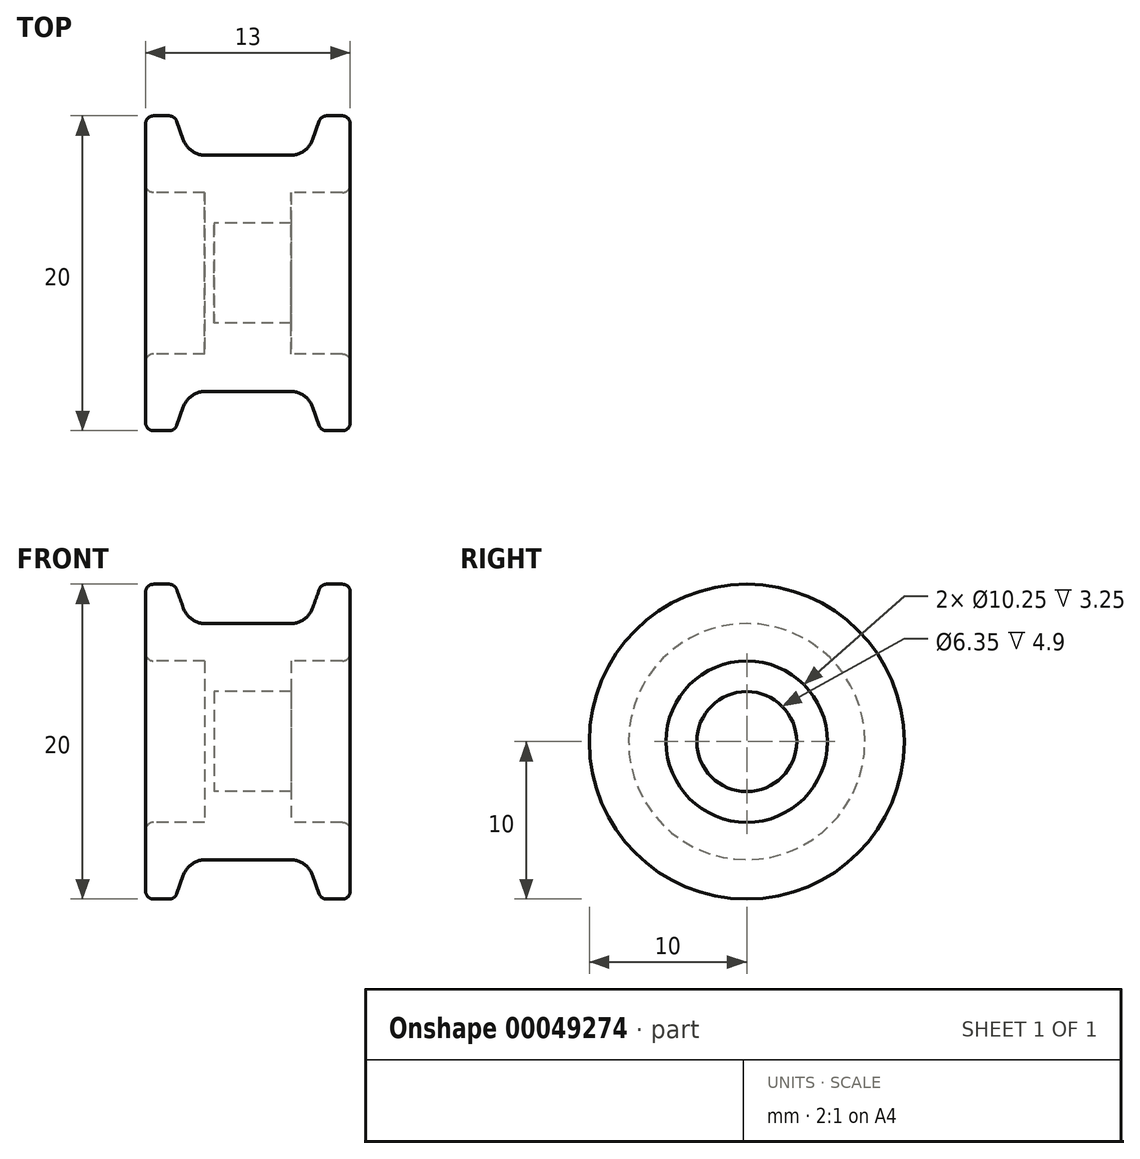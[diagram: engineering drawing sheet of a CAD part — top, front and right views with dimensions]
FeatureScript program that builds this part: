
annotation { "Feature Type Name" : "Feature", "Feature Type Description" : "" }
export const myFeature = defineFeature(function(context is Context, id is Id, definition is map)
    precondition{}
    {
        {
            var Q0;
            Q0=qCreatedBy(makeId("Front.planeOp"),FACE);
            var sketch = newSketch(context, id + "F0", { "sketchPlane" : qUnion([Q0])});
            skLineSegment(sketch, "E0", {"start": v(0, 21.72) * mm, "end": v(0, -20.37) * mm, "construction": true});
            skLineSegment(sketch, "E1", {"start": v(-6, 10) * mm, "end": v(-5, 10) * mm});
            skLineSegment(sketch, "E2", {"start": v(-6.5, 9.5) * mm, "end": v(-6.5, 5.62) * mm});
            skLineSegment(sketch, "E3", {"start": v(-6, 5.12) * mm, "end": v(-2.75, 5.12) * mm});
            skLineSegment(sketch, "E4", {"start": v(-2.75, 5.12) * mm, "end": v(-2.75, 3.17) * mm});
            skLineSegment(sketch, "E5", {"start": v(-2.75, 3.17) * mm, "end": v(0, 3.18) * mm});
            skLineSegment(sketch, "E6", {"start": v(-16, 0) * mm, "end": v(17.8, 0) * mm, "construction": true});
            skLineSegment(sketch, "E7", {"start": v(-4.53, 9.67) * mm, "end": v(-4.1, 8.5) * mm});
            skLineSegment(sketch, "E8", {"start": v(-2.7, 7.5) * mm, "end": v(0, 7.5) * mm});
            skLineSegment(sketch, "E9.bottom", {"start": v(-2.75, 3.17) * mm, "end": v(-2.15, 3.17) * mm});
            skLineSegment(sketch, "E9.left", {"start": v(-2.75, 3.17) * mm, "end": v(-2.75, 0) * mm});
            skLineSegment(sketch, "E9.right", {"start": v(-2.15, 3.17) * mm, "end": v(-2.15, 0) * mm});
            skPoint(sketch, "E10.visualSharp", {"position": v(-3.75, 7.5) * mm});
            skArc(sketch, "E10.filletArc", {"start": v(-4.1, 8.5) * mm, "mid": v(-3.56, 7.77) * mm, "end": v(-2.7, 7.5) * mm});
            skPoint(sketch, "E11.visualSharp", {"position": v(-4.65, 10) * mm});
            skArc(sketch, "E11.filletArc", {"start": v(-4.53, 9.67) * mm, "mid": v(-4.71, 9.9) * mm, "end": v(-5, 10) * mm});
            skPoint(sketch, "E12.visualSharp", {"position": v(-6.5, 5.12) * mm});
            skArc(sketch, "E12.filletArc", {"start": v(-6.5, 5.62) * mm, "mid": v(-6.35, 5.27) * mm, "end": v(-6, 5.12) * mm});
            skLineSegment(sketch, "E13.MirrorCS", {"start": v(2.7, 7.5) * mm, "end": v(0, 7.5) * mm});
            skArc(sketch, "E14.MirrorCS", {"start": v(4.1, 8.5) * mm, "mid": v(3.56, 7.77) * mm, "end": v(2.7, 7.5) * mm});
            skLineSegment(sketch, "E15.MirrorCS", {"start": v(4.53, 9.67) * mm, "end": v(4.1, 8.5) * mm});
            skArc(sketch, "E16.MirrorCS", {"start": v(4.53, 9.67) * mm, "mid": v(4.71, 9.9) * mm, "end": v(5, 10) * mm});
            skLineSegment(sketch, "E17.MirrorCS", {"start": v(6, 10) * mm, "end": v(5, 10) * mm});
            skLineSegment(sketch, "E18.MirrorCS", {"start": v(6.5, 9.5) * mm, "end": v(6.5, 5.63) * mm});
            skArc(sketch, "E19.MirrorCS", {"start": v(6.5, 5.63) * mm, "mid": v(6.35, 5.27) * mm, "end": v(6, 5.13) * mm});
            skLineSegment(sketch, "E20.MirrorCS", {"start": v(6, 5.12) * mm, "end": v(2.75, 5.12) * mm});
            skLineSegment(sketch, "E21.MirrorCS", {"start": v(2.75, 5.12) * mm, "end": v(2.75, 3.18) * mm});
            skLineSegment(sketch, "E22.MirrorCS", {"start": v(2.75, 3.18) * mm, "end": v(0, 3.18) * mm});
            skPoint(sketch, "E23.visualSharp", {"position": v(-6.5, 10) * mm});
            skArc(sketch, "E23.filletArc", {"start": v(-6, 10) * mm, "mid": v(-6.35, 9.85) * mm, "end": v(-6.5, 9.5) * mm});
            skPoint(sketch, "E24.visualSharp", {"position": v(6.5, 10) * mm});
            skArc(sketch, "E24.filletArc", {"start": v(6.5, 9.5) * mm, "mid": v(6.35, 9.85) * mm, "end": v(6, 10) * mm});
            skLineSegment(sketch, "E25", {"start": v(-2.75, 0) * mm, "end": v(-2.15, 0) * mm});
            skSolve(sketch);
        }
        {
            var Q0;
            Q0=makeQuery(id+"F0.imprint","IMPRINT",FACE,{"disambiguationData":[TD([[makeQuery(id+"F0.imprint","IMPRINT",EDGE,{"derivedFrom":sQuery(id+"F0.wireOp",EDGE,"E1")}),-1.0]])]});
            var Q1;
            {var subQ0=sQuery(id+"F0.wireOp",EDGE,"E9.left");Q1=makeQuery(id+"F0.imprint","IMPRINT",FACE,{"disambiguationData":[TD([[makeQuery(id+"F0.imprint","IMPRINT",EDGE,{"derivedFrom":subQ0}),1.0]])]});}
            var Q2;
            {var subQ2=sQuery(id+"F0.wireOp",EDGE,"2c1501b0-91c7-4a98-a6ea-ac661c5949f00.MirrorCS");Q2=makeQuery(id+"F0.imprint","IMPRINT",FACE,{"disambiguationData":[TD([[makeQuery(id+"F0.imprint","IMPRINT",EDGE,{"derivedFrom":subQ2}),1.0]])]});}
            var Q3;
            Q3=sQuery(id+"F0.wireOp",EDGE,"E6");
            revolve(context, id + "F1", {"entities" : qUnion([Q0, Q1, Q2]), "axis" : qUnion([Q3]), "revolveType" : RevolveType.FULL});
        }
    });
